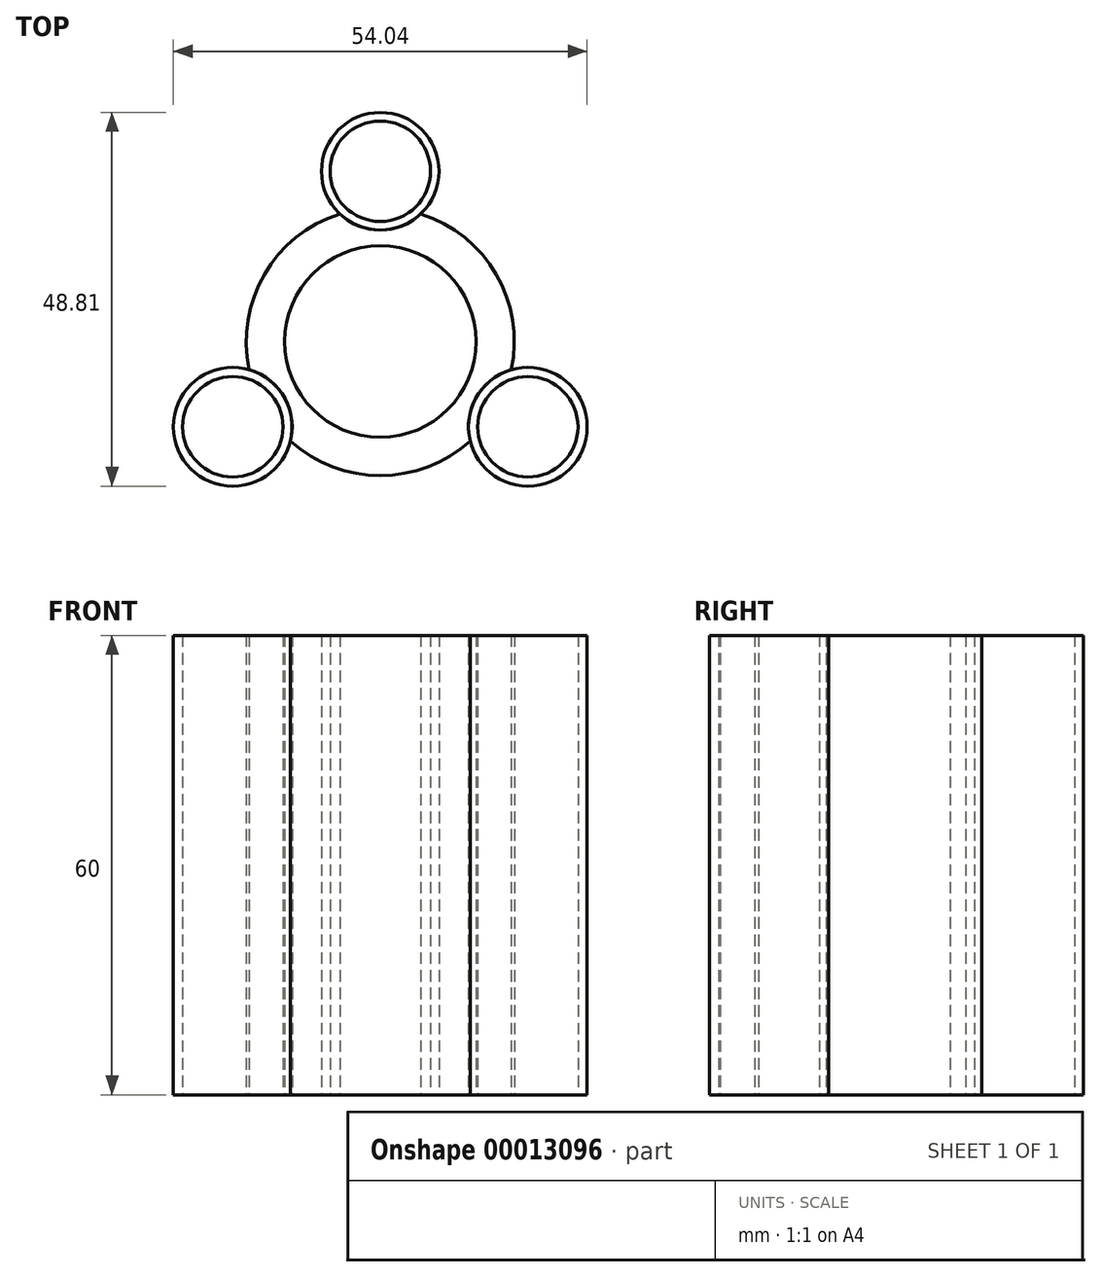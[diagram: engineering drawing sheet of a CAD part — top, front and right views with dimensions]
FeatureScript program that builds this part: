
annotation { "Feature Type Name" : "Feature", "Feature Type Description" : "" }
export const myFeature = defineFeature(function(context is Context, id is Id, definition is map)
    precondition{}
    {
        {
            var Q0;
            Q0=qCreatedBy(makeId("Top.planeOp"),FACE);
            var sketch = newSketch(context, id + "F0", { "sketchPlane" : qUnion([Q0])});
            skCircle(sketch, "E0", {"center": v(0, 0) * mm, "radius": 30 * mm, "construction": true});
            skCircle(sketch, "E1", {"center": v(0, 0) * mm, "radius": 12.5 * mm});
            skCircle(sketch, "E2", {"center": v(0, 0) * mm, "radius": 17.5 * mm});
            skPoint(sketch, "E3", {"position": v(0, 14.5) * mm});
            skPoint(sketch, "E4", {"position": v(0, 12.5) * mm});
            skLineSegment(sketch, "E5", {"start": v(0, 14.5) * mm, "end": v(0, 30) * mm, "construction": true});
            skPoint(sketch, "E6", {"position": v(0, 22.25) * mm});
            skCircle(sketch, "E7", {"center": v(0, 22.25) * mm, "radius": 7.68 * mm});
            skLineSegment(sketch, "E8", {"start": v(0, 0) * mm, "end": v(-25.98, -15) * mm, "construction": true});
            skPoint(sketch, "E9", {"position": v(-10.83, -6.25) * mm});
            skPoint(sketch, "E10", {"position": v(-12.56, -7.25) * mm});
            skPoint(sketch, "E11", {"position": v(-19.27, -11.13) * mm});
            skCircle(sketch, "E12", {"center": v(-19.27, -11.13) * mm, "radius": 7.75 * mm});
            skCircle(sketch, "E13.MirrorC", {"center": v(19.27, -11.13) * mm, "radius": 7.75 * mm});
            skLineSegment(sketch, "E14.MirrorCS", {"start": v(0, 0) * mm, "end": v(25.98, -15) * mm, "construction": true});
            skPoint(sketch, "E15", {"position": v(0, 28.8) * mm});
            skCircle(sketch, "E16", {"center": v(0, 22.25) * mm, "radius": 6.55 * mm});
            skPoint(sketch, "E17", {"position": v(-24.94, -14.4) * mm});
            skCircle(sketch, "E18", {"center": v(-19.27, -11.13) * mm, "radius": 6.55 * mm});
            skCircle(sketch, "E19.MirrorC", {"center": v(19.27, -11.13) * mm, "radius": 6.55 * mm});
            skSolve(sketch);
        }
        {
            var Q0;
            Q0=makeQuery(id+"F0.imprint","IMPRINT",FACE,{"disambiguationData":[TD([[makeQuery(id+"F0.imprint","IMPRINT",EDGE,{"derivedFrom":sQuery(id+"F0.wireOp",EDGE,"E1")}),-1.0]])]});
            extrude(context, id + "F1", {"entities" : qUnion([Q0]), "depth" : 60 * mm});
        }
        {
            var Q0;
            {var subQ1=sQuery(id+"F0.wireOp",EDGE,"E2");var subQ4=sQuery(id+"F0.wireOp",EDGE,"E7");var subQ6=makeQuery(id+"F0.imprint","INTERSECT",VERTEX,{"disambiguationData":[OD(0.0)],"derivedFrom":[subQ1,subQ4]});Q0=makeQuery(id+"F0.imprint","IMPRINT",FACE,{"disambiguationData":[TD([[makeQuery(id+"F0.imprint","IMPRINT",EDGE,{"disambiguationData":[TD([[subQ6,-1.0]])],"derivedFrom":subQ1}),-1.0]])]});}
            var Q1;
            {var subQ0=sQuery(id+"F0.wireOp",EDGE,"E7");var subQ1=sQuery(id+"F0.wireOp",EDGE,"E2");var subQ3=makeQuery(id+"F0.imprint","INTERSECT",VERTEX,{"disambiguationData":[OD(0.0)],"derivedFrom":[subQ1,subQ0]});Q1=makeQuery(id+"F0.imprint","IMPRINT",FACE,{"disambiguationData":[TD([[makeQuery(id+"F0.imprint","IMPRINT",EDGE,{"disambiguationData":[TD([[subQ3,-1.0]])],"derivedFrom":subQ1}),1.0]])]});}
            extrude(context, id + "F2", {"entities" : qUnion([Q0, Q1]), "depth" : 60 * mm});
        }
        {
            var Q0;
            {var subQ1=sQuery(id+"F0.wireOp",EDGE,"E2");var subQ4=sQuery(id+"F0.wireOp",EDGE,"E12");var subQ6=makeQuery(id+"F0.imprint","INTERSECT",VERTEX,{"disambiguationData":[OD(0.0)],"derivedFrom":[subQ1,subQ4]});Q0=makeQuery(id+"F0.imprint","IMPRINT",FACE,{"disambiguationData":[TD([[makeQuery(id+"F0.imprint","IMPRINT",EDGE,{"disambiguationData":[TD([[subQ6,-1.0]])],"derivedFrom":subQ1}),-1.0]])]});}
            var Q1;
            {var subQ1=sQuery(id+"F0.wireOp",EDGE,"E2");var subQ4=sQuery(id+"F0.wireOp",EDGE,"E12");var subQ6=makeQuery(id+"F0.imprint","INTERSECT",VERTEX,{"disambiguationData":[OD(0.0)],"derivedFrom":[subQ1,subQ4]});Q1=makeQuery(id+"F0.imprint","IMPRINT",FACE,{"disambiguationData":[TD([[makeQuery(id+"F0.imprint","IMPRINT",EDGE,{"disambiguationData":[TD([[subQ6,-1.0]])],"derivedFrom":subQ1}),1.0]])]});}
            extrude(context, id + "F3", {"entities" : qUnion([Q0, Q1]), "depth" : 60 * mm});
        }
        {
            var Q0;
            {var subQ1=sQuery(id+"F0.wireOp",EDGE,"E2");var subQ4=sQuery(id+"F0.wireOp",EDGE,"E13.MirrorC");var subQ6=makeQuery(id+"F0.imprint","INTERSECT",VERTEX,{"disambiguationData":[OD(0.0)],"derivedFrom":[subQ1,subQ4]});Q0=makeQuery(id+"F0.imprint","IMPRINT",FACE,{"disambiguationData":[TD([[makeQuery(id+"F0.imprint","IMPRINT",EDGE,{"disambiguationData":[TD([[subQ6,-1.0]])],"derivedFrom":subQ1}),-1.0]])]});}
            var Q1;
            {var subQ1=sQuery(id+"F0.wireOp",EDGE,"E2");var subQ4=sQuery(id+"F0.wireOp",EDGE,"E13.MirrorC");var subQ6=makeQuery(id+"F0.imprint","INTERSECT",VERTEX,{"disambiguationData":[OD(0.0)],"derivedFrom":[subQ1,subQ4]});Q1=makeQuery(id+"F0.imprint","IMPRINT",FACE,{"disambiguationData":[TD([[makeQuery(id+"F0.imprint","IMPRINT",EDGE,{"disambiguationData":[TD([[subQ6,-1.0]])],"derivedFrom":subQ1}),1.0]])]});}
            extrude(context, id + "F4", {"entities" : qUnion([Q0, Q1]), "depth" : 60 * mm});
        }
    });
